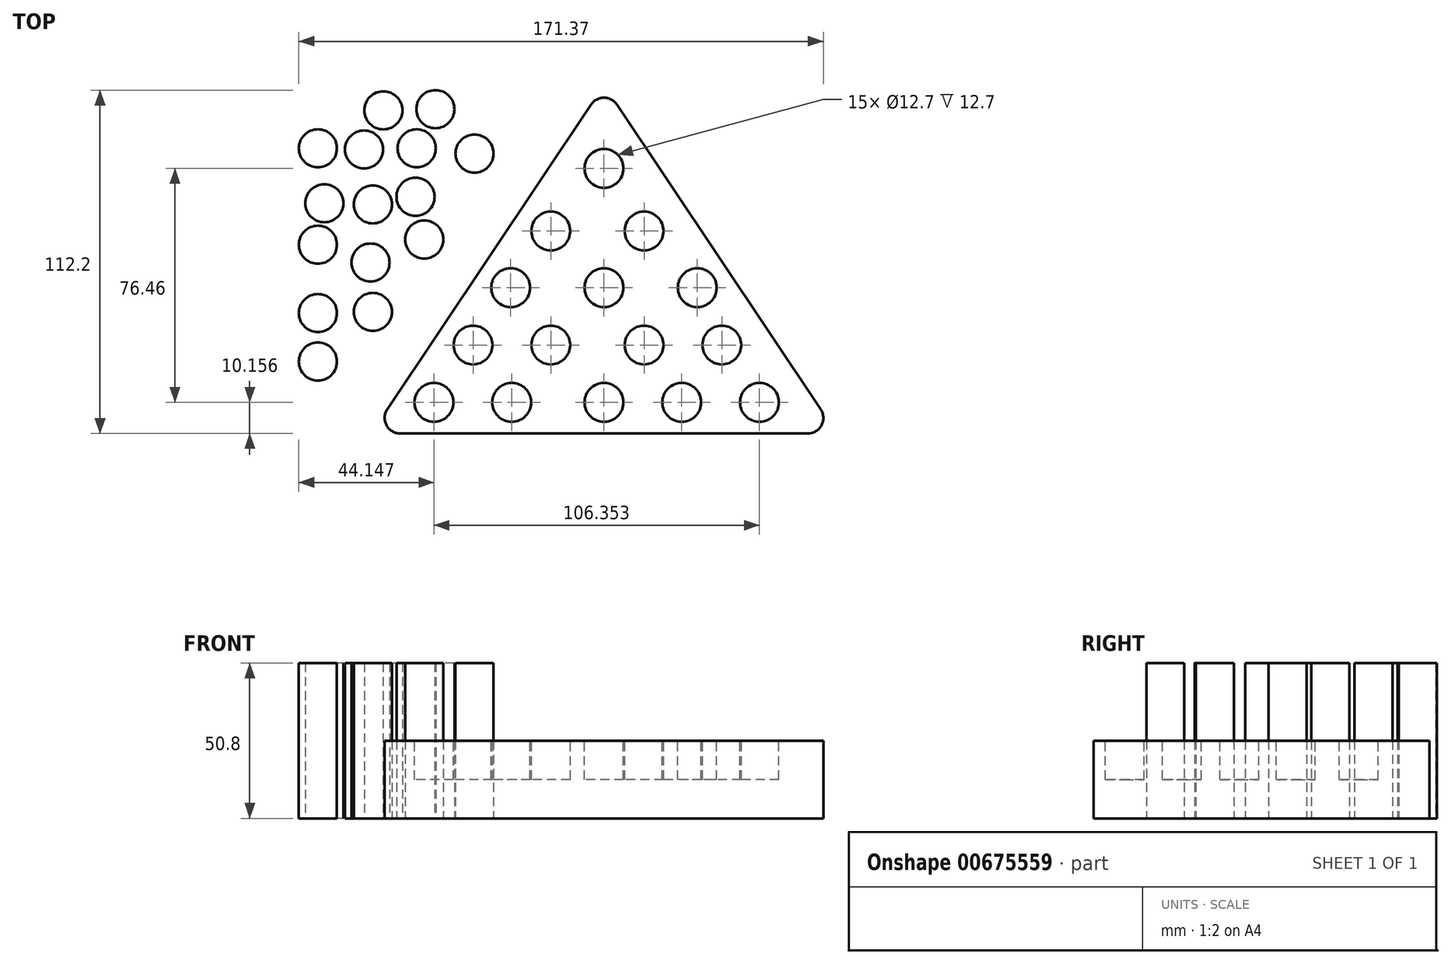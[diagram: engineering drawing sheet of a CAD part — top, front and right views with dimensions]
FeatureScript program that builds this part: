
annotation { "Feature Type Name" : "Feature", "Feature Type Description" : "" }
export const myFeature = defineFeature(function(context is Context, id is Id, definition is map)
    precondition{}
    {
        {
            var Q0;
            Q0=qCreatedBy(makeId("Top.planeOp"),FACE);
            var sketch = newSketch(context, id + "F0", { "sketchPlane" : qUnion([Q0])});
            skLineSegment(sketch, "E0", {"start": v(-76.1, -55.85) * mm, "end": v(76.1, -55.85) * mm});
            skLineSegment(sketch, "E1", {"start": v(76.1, -55.85) * mm, "end": v(0, 57.95) * mm});
            skLineSegment(sketch, "E2", {"start": v(0, 57.95) * mm, "end": v(-76.1, -55.85) * mm});
            skSolve(sketch);
        }
        {
            var Q0;
            Q0=makeQuery(id+"F0.imprint","IMPRINT",FACE,{"disambiguationData":[TD([[makeQuery(id+"F0.imprint","IMPRINT",EDGE,{"derivedFrom":sQuery(id+"F0.wireOp",EDGE,"E0")}),1.0]])]});
            extrude(context, id + "F1", {"entities" : qUnion([Q0]), "depth" : 25.4 * mm, "offsetDistance" : 25.4 * mm});
        }
        {
            var Q0;
            Q0=makeQuery(id+"F1.opExtrude","CAP_FACE",FACE,{"disambiguationData":[OSD([sQuery(id+"F0.wireOp",EDGE,"E0"),sQuery(id+"F0.wireOp",EDGE,"E1"),sQuery(id+"F0.wireOp",EDGE,"E2")])],"isStart":false});
            var sketch = newSketch(context, id + "F2", { "sketchPlane" : qUnion([Q0])});
            skCircle(sketch, "E3", {"center": v(0, -45.7) * mm, "radius": 6.35 * mm});
            skCircle(sketch, "E4", {"center": v(-30.15, -45.7) * mm, "radius": 6.35 * mm});
            skCircle(sketch, "E5", {"center": v(-55.55, -45.7) * mm, "radius": 6.35 * mm});
            skCircle(sketch, "E6", {"center": v(25.4, -45.7) * mm, "radius": 6.35 * mm});
            skCircle(sketch, "E7", {"center": v(50.8, -45.7) * mm, "radius": 6.35 * mm});
            skSolve(sketch);
        }
        {
            var Q0;
            Q0=makeQuery(id+"F2.imprint","IMPRINT",FACE,{"disambiguationData":[TD([[makeQuery(id+"F2.imprint","IMPRINT",EDGE,{"derivedFrom":sQuery(id+"F2.wireOp",EDGE,"E3")}),-1.0]])]});
            var sketch = newSketch(context, id + "F3", { "sketchPlane" : qUnion([Q0])});
            skCircle(sketch, "E8", {"center": v(-42.8, -26.95) * mm, "radius": 6.35 * mm});
            skCircle(sketch, "E9", {"center": v(-17.4, -26.95) * mm, "radius": 6.35 * mm});
            skCircle(sketch, "E10", {"center": v(13.09, -26.95) * mm, "radius": 6.35 * mm});
            skCircle(sketch, "E11", {"center": v(38.49, -26.95) * mm, "radius": 6.35 * mm});
            skCircle(sketch, "E12", {"center": v(0, -8.21) * mm, "radius": 6.35 * mm});
            skCircle(sketch, "E13", {"center": v(-30.48, -8.21) * mm, "radius": 6.35 * mm});
            skCircle(sketch, "E14", {"center": v(30.48, -8.21) * mm, "radius": 6.35 * mm});
            skCircle(sketch, "E15", {"center": v(13.09, 10.3) * mm, "radius": 6.35 * mm});
            skCircle(sketch, "E16", {"center": v(-17.4, 10.3) * mm, "radius": 6.35 * mm});
            skCircle(sketch, "E17", {"center": v(0, 30.77) * mm, "radius": 6.35 * mm});
            skSolve(sketch);
        }
        {
            var Q0;
            Q0 = qSketchRegion(id + "F3", true);
            var Q1;
            Q1=makeQuery(id+"F2.imprint","IMPRINT",FACE,{"disambiguationData":[TD([[makeQuery(id+"F2.imprint","IMPRINT",EDGE,{"derivedFrom":sQuery(id+"F2.wireOp",EDGE,"E5")}),1.0]])]});
            var Q2;
            Q2=makeQuery(id+"F2.imprint","IMPRINT",FACE,{"disambiguationData":[TD([[makeQuery(id+"F2.imprint","IMPRINT",EDGE,{"derivedFrom":sQuery(id+"F2.wireOp",EDGE,"E4")}),1.0]])]});
            var Q3;
            Q3=makeQuery(id+"F2.imprint","IMPRINT",FACE,{"disambiguationData":[TD([[makeQuery(id+"F2.imprint","IMPRINT",EDGE,{"derivedFrom":sQuery(id+"F2.wireOp",EDGE,"E3")}),1.0]])]});
            var Q4;
            Q4=makeQuery(id+"F2.imprint","IMPRINT",FACE,{"disambiguationData":[TD([[makeQuery(id+"F2.imprint","IMPRINT",EDGE,{"derivedFrom":sQuery(id+"F2.wireOp",EDGE,"E7")}),1.0]])]});
            var Q5;
            Q5=makeQuery(id+"F2.imprint","IMPRINT",FACE,{"disambiguationData":[TD([[makeQuery(id+"F2.imprint","IMPRINT",EDGE,{"derivedFrom":sQuery(id+"F2.wireOp",EDGE,"E6")}),1.0]])]});
            extrude(context, id + "F4", {"entities" : qUnion([Q0, Q1, Q2, Q3, Q4, Q5]), "operationType" : NewBodyOperationType.REMOVE, "oppositeDirection" : true, "depth" : 12.7 * mm, "offsetDistance" : 25.4 * mm});
        }
        {
            var Q0;
            Q0=qCreatedBy(makeId("Top.planeOp"),FACE);
            var sketch = newSketch(context, id + "F5", { "sketchPlane" : qUnion([Q0])});
            skCircle(sketch, "E18", {"center": v(-72.09, 49.74) * mm, "radius": 6.22 * mm});
            skCircle(sketch, "E19", {"center": v(-55.1, 50.13) * mm, "radius": 6.22 * mm});
            skCircle(sketch, "E20", {"center": v(-93.47, 37.33) * mm, "radius": 6.22 * mm});
            skCircle(sketch, "E21", {"center": v(-78.39, 36.95) * mm, "radius": 6.22 * mm});
            skCircle(sketch, "E22", {"center": v(-61.2, 37.33) * mm, "radius": 6.22 * mm});
            skCircle(sketch, "E23", {"center": v(-42.3, 35.61) * mm, "radius": 6.22 * mm});
            skCircle(sketch, "E24", {"center": v(-91.37, 19.38) * mm, "radius": 6.22 * mm});
            skCircle(sketch, "E25", {"center": v(-75.52, 19) * mm, "radius": 6.22 * mm});
            skCircle(sketch, "E26", {"center": v(-61.58, 21.48) * mm, "radius": 6.22 * mm});
            skCircle(sketch, "E27", {"center": v(-93.47, 5.82) * mm, "radius": 6.22 * mm});
            skCircle(sketch, "E28", {"center": v(-76.29, 0) * mm, "radius": 6.22 * mm});
            skCircle(sketch, "E29", {"center": v(-58.72, 7.54) * mm, "radius": 6.22 * mm});
            skCircle(sketch, "E30", {"center": v(-93.47, -16.52) * mm, "radius": 6.22 * mm});
            skCircle(sketch, "E31", {"center": v(-75.52, -16.14) * mm, "radius": 6.22 * mm});
            skCircle(sketch, "E32", {"center": v(-93.47, -32.37) * mm, "radius": 6.22 * mm});
            skSolve(sketch);
        }
        {
            var Q0;
            Q0=makeQuery(id+"F5.imprint","IMPRINT",FACE,{"disambiguationData":[TD([[makeQuery(id+"F5.imprint","IMPRINT",EDGE,{"derivedFrom":sQuery(id+"F5.wireOp",EDGE,"E18")}),1.0]])]});
            var Q1;
            Q1=makeQuery(id+"F5.imprint","IMPRINT",FACE,{"disambiguationData":[TD([[makeQuery(id+"F5.imprint","IMPRINT",EDGE,{"derivedFrom":sQuery(id+"F5.wireOp",EDGE,"E19")}),1.0]])]});
            var Q2;
            Q2=makeQuery(id+"F5.imprint","IMPRINT",FACE,{"disambiguationData":[TD([[makeQuery(id+"F5.imprint","IMPRINT",EDGE,{"derivedFrom":sQuery(id+"F5.wireOp",EDGE,"E23")}),1.0]])]});
            var Q3;
            Q3=makeQuery(id+"F5.imprint","IMPRINT",FACE,{"disambiguationData":[TD([[makeQuery(id+"F5.imprint","IMPRINT",EDGE,{"derivedFrom":sQuery(id+"F5.wireOp",EDGE,"E22")}),1.0]])]});
            var Q4;
            Q4=makeQuery(id+"F5.imprint","IMPRINT",FACE,{"disambiguationData":[TD([[makeQuery(id+"F5.imprint","IMPRINT",EDGE,{"derivedFrom":sQuery(id+"F5.wireOp",EDGE,"E21")}),1.0]])]});
            var Q5;
            Q5=makeQuery(id+"F5.imprint","IMPRINT",FACE,{"disambiguationData":[TD([[makeQuery(id+"F5.imprint","IMPRINT",EDGE,{"derivedFrom":sQuery(id+"F5.wireOp",EDGE,"E20")}),1.0]])]});
            var Q6;
            Q6=makeQuery(id+"F5.imprint","IMPRINT",FACE,{"disambiguationData":[TD([[makeQuery(id+"F5.imprint","IMPRINT",EDGE,{"derivedFrom":sQuery(id+"F5.wireOp",EDGE,"E24")}),1.0]])]});
            var Q7;
            Q7=makeQuery(id+"F5.imprint","IMPRINT",FACE,{"disambiguationData":[TD([[makeQuery(id+"F5.imprint","IMPRINT",EDGE,{"derivedFrom":sQuery(id+"F5.wireOp",EDGE,"E25")}),1.0]])]});
            var Q8;
            Q8=makeQuery(id+"F5.imprint","IMPRINT",FACE,{"disambiguationData":[TD([[makeQuery(id+"F5.imprint","IMPRINT",EDGE,{"derivedFrom":sQuery(id+"F5.wireOp",EDGE,"E26")}),1.0]])]});
            var Q9;
            Q9=makeQuery(id+"F5.imprint","IMPRINT",FACE,{"disambiguationData":[TD([[makeQuery(id+"F5.imprint","IMPRINT",EDGE,{"derivedFrom":sQuery(id+"F5.wireOp",EDGE,"E29")}),1.0]])]});
            var Q10;
            Q10=makeQuery(id+"F5.imprint","IMPRINT",FACE,{"disambiguationData":[TD([[makeQuery(id+"F5.imprint","IMPRINT",EDGE,{"derivedFrom":sQuery(id+"F5.wireOp",EDGE,"E28")}),1.0]])]});
            var Q11;
            Q11=makeQuery(id+"F5.imprint","IMPRINT",FACE,{"disambiguationData":[TD([[makeQuery(id+"F5.imprint","IMPRINT",EDGE,{"derivedFrom":sQuery(id+"F5.wireOp",EDGE,"E27")}),1.0]])]});
            var Q12;
            Q12=makeQuery(id+"F5.imprint","IMPRINT",FACE,{"disambiguationData":[TD([[makeQuery(id+"F5.imprint","IMPRINT",EDGE,{"derivedFrom":sQuery(id+"F5.wireOp",EDGE,"E30")}),1.0]])]});
            var Q13;
            Q13=makeQuery(id+"F5.imprint","IMPRINT",FACE,{"disambiguationData":[TD([[makeQuery(id+"F5.imprint","IMPRINT",EDGE,{"derivedFrom":sQuery(id+"F5.wireOp",EDGE,"E31")}),1.0]])]});
            var Q14;
            Q14=makeQuery(id+"F5.imprint","IMPRINT",FACE,{"disambiguationData":[TD([[makeQuery(id+"F5.imprint","IMPRINT",EDGE,{"derivedFrom":sQuery(id+"F5.wireOp",EDGE,"E32")}),1.0]])]});
            extrude(context, id + "F6", {"entities" : qUnion([Q0, Q1, Q2, Q3, Q4, Q5, Q6, Q7, Q8, Q9, Q10, Q11, Q12, Q13, Q14]), "depth" : 50.8 * mm, "offsetDistance" : 25.4 * mm});
        }
        {
            var Q0;
            Q0=makeQuery(id+"F1.opExtrude","SWEPT_EDGE",EDGE,{"disambiguationData":[OSD([sQuery(id+"F0.wireOp",EDGE,"E0"),sQuery(id+"F0.wireOp",EDGE,"E1")])]});
            var Q1;
            Q1=makeQuery(id+"F1.opExtrude","SWEPT_EDGE",EDGE,{"disambiguationData":[OSD([sQuery(id+"F0.wireOp",EDGE,"E0"),sQuery(id+"F0.wireOp",EDGE,"E2")])]});
            var Q2;
            Q2=makeQuery(id+"F1.opExtrude","SWEPT_EDGE",EDGE,{"disambiguationData":[OSD([sQuery(id+"F0.wireOp",EDGE,"E1"),sQuery(id+"F0.wireOp",EDGE,"E2")])]});
            fillet(context, id + "F7", {"entities" : qUnion([Q0, Q1, Q2]), "radius" : 5.08 * mm, "tangentPropagation" : true, "allowEdgeOverflow" : false});
        }
    });
